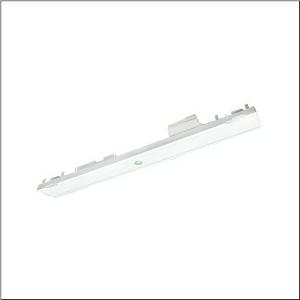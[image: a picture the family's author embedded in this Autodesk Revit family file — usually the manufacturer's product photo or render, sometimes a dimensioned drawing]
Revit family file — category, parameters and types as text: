
# Revit family: licross_r_56tl157c4x31_efa4
name_source: partatom
category: Lighting Fixtures
units: mm (PartAtom-declared; Revit-internal decimal feet)

## family parameters
Cut with Voids When Loaded = No
Host = Face
Light Source = No
Part Type = Normal
Room Calculation Point = No
Round Connector Dimension = Use Diameter
Shared = No

## types (1)
- Licross® (1 x LED, 320 lm, 3.9 W, 4000K)
    Apparent Load = 4 VA
    CIE Flux Codes = 31 68 99 100 100
    Color Rendering = 70
    Color Temperature = 4000K
    Default Elevation = 1800 mm
    Description = Licross®, luminaire insert, of sheet steel, coil coated, white, length: 500mm, width: 59mm, height: 60mm, mounting height: 2.5..7m, emergency light element,LED rated luminous flux: 320lm, light colour: 740, control gear: CEAG, with plug, 6-pole, with phase selection, mains connection: 220..240V, AC/DC, 0/50..60Hz, rated input power: 3.9W, internal wiring halogen-free, for trunking rail, 9..14-core, for emergency light function, supply monitoring module CEAG, with address switch, choice between two emergency light lines via tool-free moving of contact pin prior to installation in trunking rail, primary light control with lens, of PMMA, primary optical cover: cover, of PMMA, light emission: direct distribution, primary light characteristic: symmetric,  for area, compatible with all CEAG STAR technology systems (ZB-S, DG-S (DualGuard-S), LP-STAR, AT-S+), protection rating (complete): IP40, insulation class (complete): insulation class I (protective earthing), certification: CE, UKCA, protection symbol: D if used in an environment without relevant dust loads, impact resistance: IK06, permissible ambient temperature for indoor applications: -20..+40°C, packaging unit: 1 piece
    Height = 60 mm  [stored 0.19685 ft]
    Lamp = 1 x LED
    Lamp Light Flux = 320 lm
    Lamp Power = 3.9 W
    Lamp count = 1
    Length = 500 mm
    Luminous efficacy = 82 lm/W
    Manufacturer = Siteco
    ModVariant = No
    Model = 56TL157C4X31
    Mounting Place = Ceiling
    Mounting Type = Pendant
    Number of Poles = 1
    OnlyDefault = Yes
    Power Factor = 1
    Product Name = Licross®
    Product group = luminaire insert | ceiling pendant
    ProductGroupID = 902
    Protection Class = Protection class I
    Protection Degree = IP 40
    RLX_Detail_Level = 1
    RLX_Emergency_Light_Flux = 0 lm
    RLX_Emergency_Type = 0
    RLX_Emergency_Type_DB = No
    RlxData = <blob elided: 14377 chars, md5=244461d0>
    Socket = socket
    Standby Power = 0 W
    System Light Flux = 320 lm
    System Power = 4 W
    Type Comments = Product without accessories
    Type Image = l_1251804.jpg
    URL = http://relux.com
    VarID = ---
    Voltage = 0 V
    Weight = 0.00 kg
    Width = 59 mm

note: [stored X ft] marks values corroborated as IEEE doubles in the binary element streams (Revit-internal decimal feet)

## geometry (parser evidence)
native form markers: Sweep x10
no freeform markers — native parametric forms only
